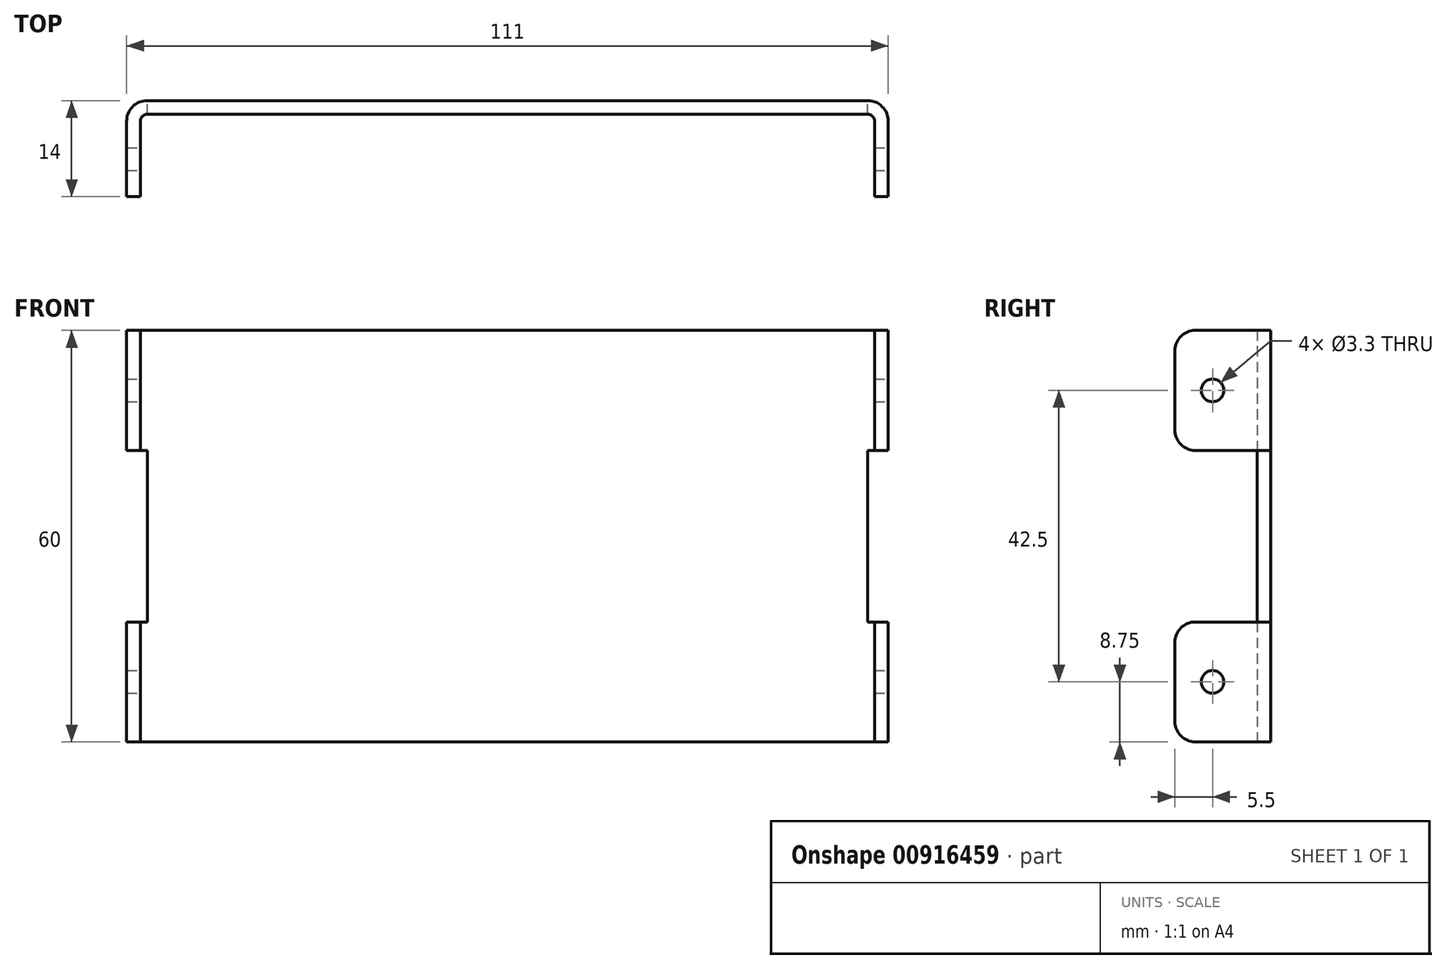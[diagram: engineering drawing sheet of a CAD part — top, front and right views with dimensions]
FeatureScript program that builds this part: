
annotation { "Feature Type Name" : "Feature", "Feature Type Description" : "" }
export const myFeature = defineFeature(function(context is Context, id is Id, definition is map)
    precondition{}
    {
        {
            var Q0;
            Q0=qCreatedBy(makeId("Top.planeOp"),FACE);
            var sketch = newSketch(context, id + "F0", { "sketchPlane" : qUnion([Q0])});
            skLineSegment(sketch, "E0", {"start": v(52.5, 0) * mm, "end": v(-52.5, 0) * mm});
            skLineSegment(sketch, "E1", {"start": v(-53.5, -1) * mm, "end": v(-53.5, -12) * mm});
            skLineSegment(sketch, "E2", {"start": v(53.5, -1) * mm, "end": v(53.5, -12) * mm});
            skPoint(sketch, "E3", {"position": v(0, 0) * mm});
            skPoint(sketch, "E4.visualSharp", {"position": v(-53.5, 0) * mm});
            skArc(sketch, "E4.filletArc", {"start": v(-52.5, 0) * mm, "mid": v(-53.2, -0.3) * mm, "end": v(-53.5, -1) * mm});
            skPoint(sketch, "E5.visualSharp", {"position": v(53.5, 0) * mm});
            skArc(sketch, "E5.filletArc", {"start": v(53.5, -1) * mm, "mid": v(53.2, -0.3) * mm, "end": v(52.5, 0) * mm});
            skLineSegment(sketch, "E6.0", {"start": v(-55.5, -1) * mm, "end": v(-55.5, -12) * mm});
            skLineSegment(sketch, "E6.1", {"start": v(55.5, -1) * mm, "end": v(55.5, -12) * mm});
            skArc(sketch, "E6.2", {"start": v(55.5, -1) * mm, "mid": v(54.62, 1.12) * mm, "end": v(52.5, 2) * mm});
            skLineSegment(sketch, "E6.3", {"start": v(52.5, 2) * mm, "end": v(-52.5, 2) * mm});
            skArc(sketch, "E6.4", {"start": v(-52.5, 2) * mm, "mid": v(-54.62, 1.12) * mm, "end": v(-55.5, -1) * mm});
            skLineSegment(sketch, "E7", {"start": v(-55.5, -12) * mm, "end": v(-53.5, -12) * mm});
            skLineSegment(sketch, "E8", {"start": v(53.5, -12) * mm, "end": v(55.5, -12) * mm});
            skSolve(sketch);
        }
        {
            var Q0;
            Q0=makeQuery(id+"F0.imprint","IMPRINT",FACE,{"disambiguationData":[TD([[makeQuery(id+"F0.imprint","IMPRINT",EDGE,{"derivedFrom":sQuery(id+"F0.wireOp",EDGE,"E0")}),-1.0]])]});
            extrude(context, id + "F1", {"entities" : qUnion([Q0]), "endBound" : BoundingType.SYMMETRIC, "depth" : 60 * mm});
        }
        {
            var Q0;
            Q0=makeQuery(id+"F1.opExtrude","SWEPT_FACE",FACE,{"disambiguationData":[OSD([sQuery(id+"F0.wireOp",EDGE,"E6.3")])]});
            var sketch = newSketch(context, id + "F2", { "sketchPlane" : qUnion([Q0])});
            skLineSegment(sketch, "E9.0", {"start": v(-55.5, 30) * mm, "end": v(-55.5, -30) * mm, "construction": true});
            skLineSegment(sketch, "E10.0", {"start": v(55.5, 30) * mm, "end": v(55.5, -30) * mm, "construction": true});
            skLineSegment(sketch, "E11.bottom", {"start": v(-55.5, 12.5) * mm, "end": v(-52.5, 12.5) * mm});
            skLineSegment(sketch, "E11.top", {"start": v(-55.5, -12.5) * mm, "end": v(-52.5, -12.5) * mm});
            skLineSegment(sketch, "E11.left", {"start": v(-55.5, 12.5) * mm, "end": v(-55.5, -12.5) * mm});
            skLineSegment(sketch, "E11.right", {"start": v(-52.5, 12.5) * mm, "end": v(-52.5, -12.5) * mm});
            skPoint(sketch, "E12", {"position": v(-52.5, 0) * mm});
            skLineSegment(sketch, "E13.MirrorCS", {"start": v(55.5, 12.5) * mm, "end": v(52.5, 12.5) * mm});
            skLineSegment(sketch, "E14.MirrorCS", {"start": v(55.5, -12.5) * mm, "end": v(52.5, -12.5) * mm});
            skPoint(sketch, "E15.MirrorP", {"position": v(52.5, 0) * mm});
            skLineSegment(sketch, "E16.MirrorCS", {"start": v(55.5, 12.5) * mm, "end": v(55.5, -12.5) * mm});
            skLineSegment(sketch, "E17.MirrorCS", {"start": v(52.5, 12.5) * mm, "end": v(52.5, -12.5) * mm});
            skPoint(sketch, "E18", {"position": v(0, 26) * mm});
            skLineSegment(sketch, "E19.bottom", {"start": v(-21.81, 24.35) * mm, "end": v(-9.8, 24.35) * mm});
            skLineSegment(sketch, "E19.top", {"start": v(-21.81, 13.85) * mm, "end": v(-9.8, 13.85) * mm});
            skLineSegment(sketch, "E19.left", {"start": v(-21.81, 24.35) * mm, "end": v(-21.81, 13.85) * mm});
            skLineSegment(sketch, "E19.right", {"start": v(-9.8, 24.35) * mm, "end": v(-9.8, 13.85) * mm});
            skLineSegment(sketch, "E20.bottom", {"start": v(9.8, 24.35) * mm, "end": v(18.96, 24.35) * mm});
            skLineSegment(sketch, "E20.top", {"start": v(9.81, 13.15) * mm, "end": v(18.96, 13.15) * mm});
            skLineSegment(sketch, "E20.left", {"start": v(9.8, 24.35) * mm, "end": v(9.81, 13.15) * mm});
            skLineSegment(sketch, "E20.right", {"start": v(18.96, 24.35) * mm, "end": v(18.96, 13.15) * mm});
            skPoint(sketch, "E21", {"position": v(0, 24.35) * mm});
            skLineSegment(sketch, "E22.bottom", {"start": v(-24.61, 11.55) * mm, "end": v(27.62, 11.55) * mm});
            skLineSegment(sketch, "E22.top", {"start": v(-24.61, 1.55) * mm, "end": v(27.62, 1.55) * mm});
            skLineSegment(sketch, "E22.left", {"start": v(-24.61, 11.55) * mm, "end": v(-24.61, 1.55) * mm});
            skLineSegment(sketch, "E22.right", {"start": v(27.62, 11.55) * mm, "end": v(27.62, 1.55) * mm});
            skSolve(sketch);
        }
        {
            var Q0;
            Q0=makeQuery(id+"F2.imprint","IMPRINT",FACE,{"disambiguationData":[TD([[makeQuery(id+"F2.imprint","IMPRINT",EDGE,{"derivedFrom":sQuery(id+"F2.wireOp",EDGE,"E11.bottom")}),-1.0]])]});
            var Q1;
            Q1=makeQuery(id+"F2.imprint","IMPRINT",FACE,{"disambiguationData":[TD([[makeQuery(id+"F2.imprint","IMPRINT",EDGE,{"derivedFrom":sQuery(id+"F2.wireOp",EDGE,"E13.MirrorCS")}),1.0]])]});
            var Q2;
            Q2=makeQuery(id+"F1.opExtrude","SWEPT_FACE",FACE,{"disambiguationData":[OSD([sQuery(id+"F0.wireOp",EDGE,"E0")])]});
            extrude(context, id + "F3", {"entities" : qUnion([Q0, Q1, Q2]), "operationType" : NewBodyOperationType.REMOVE, "endBound" : BoundingType.THROUGH_ALL, "oppositeDirection" : true, "offsetDistance" : 25 * mm, "depth" : 25 * mm});
        }
        {
            var Q0;
            {var subQ2=sQuery(id+"F0.wireOp",EDGE,"E6.1");Q0=makeQuery(id+"F3.boolean.opBoolean","SPLIT",FACE,{"disambiguationData":[TD([makeQuery(id+"F3.opExtrude","SWEPT_FACE",FACE,{"disambiguationData":[OSD([sQuery(id+"F2.wireOp",EDGE,"E11.bottom")])]})])],"derivedFrom":makeQuery(id+"F1.opExtrude","SWEPT_FACE",FACE,{"disambiguationData":[OSD([subQ2])]})});}
            var sketch = newSketch(context, id + "F4", { "sketchPlane" : qUnion([Q0])});
            skLineSegment(sketch, "E23", {"start": v(-1, 12.5) * mm, "end": v(-12, 30) * mm, "construction": true});
            skLineSegment(sketch, "E24.0.0", {"start": v(-1, -12.5) * mm, "end": v(-12, -12.5) * mm, "construction": true});
            skLineSegment(sketch, "E24.0.1", {"start": v(-12, -12.5) * mm, "end": v(-12, -30) * mm, "construction": true});
            skLineSegment(sketch, "E24.0.2", {"start": v(-12, -30) * mm, "end": v(-1, -30) * mm, "construction": true});
            skLineSegment(sketch, "E24.0.3", {"start": v(-1, -30) * mm, "end": v(-1, -12.5) * mm, "construction": true});
            skLineSegment(sketch, "E25", {"start": v(-1, -30) * mm, "end": v(-12, -12.5) * mm, "construction": true});
            skPoint(sketch, "E26", {"position": v(-6.5, 21.25) * mm});
            skPoint(sketch, "E27", {"position": v(-6.5, -21.25) * mm});
            skSolve(sketch);
        }
        {
            var Q0;
            Q0=sQuery(id+"F4.wireOp",VERTEX,"E26");
            var Q1;
            Q1=sQuery(id+"F4.wireOp",VERTEX,"E27");
            var Q2;
            Q2=makeQuery(id+"F1.opExtrude","SWEPT_BODY",BODY,{"disambiguationData":[OSD([sQuery(id+"F0.wireOp",EDGE,"E0"),sQuery(id+"F0.wireOp",EDGE,"E1"),sQuery(id+"F0.wireOp",EDGE,"E2"),sQuery(id+"F0.wireOp",EDGE,"E4.filletArc"),sQuery(id+"F0.wireOp",EDGE,"E5.filletArc"),sQuery(id+"F0.wireOp",EDGE,"E6.0"),sQuery(id+"F0.wireOp",EDGE,"E6.1"),sQuery(id+"F0.wireOp",EDGE,"E6.2"),sQuery(id+"F0.wireOp",EDGE,"E6.3"),sQuery(id+"F0.wireOp",EDGE,"E6.4"),sQuery(id+"F0.wireOp",EDGE,"E7"),sQuery(id+"F0.wireOp",EDGE,"E8")])]});
            hole(context, id + "F5", {"style" : HoleStyle.SIMPLE, "endStyle" : HoleEndStyle.THROUGH, "standardTappedOrClearance" : lookupTablePath({ "standard" : "ISO", "fit" : "Normal", "size" : "M3", "type" : "Clearance" }), "standardBlindInLast" : lookupTablePath({ "fit" : "Standard", "standard" : "ISO", "size" : "M3", "type" : "Clearance" }), "holeDiameter" : 3.3 * mm, "tappedDepth" : 12 * mm, "tapClearance" : 3, "locations" : qUnion([Q0, Q1]), "scope" : qUnion([Q2])});
        }
        {
            var Q0;
            Q0=makeQuery(id+"F1.opExtrude","CAP_EDGE",EDGE,{"disambiguationData":[OSD([sQuery(id+"F0.wireOp",EDGE,"E7")])],"isStart":false});
            var Q1;
            Q1=makeQuery(id+"F3.boolean.opBoolean","INTERSECT",EDGE,{"derivedFrom":[makeQuery(id+"F1.opExtrude","SWEPT_FACE",FACE,{"disambiguationData":[OSD([sQuery(id+"F0.wireOp",EDGE,"E7")])]}),makeQuery(id+"F3.opExtrude","SWEPT_FACE",FACE,{"disambiguationData":[OSD([sQuery(id+"F2.wireOp",EDGE,"E13.MirrorCS")])]})]});
            var Q2;
            Q2=makeQuery(id+"F3.boolean.opBoolean","INTERSECT",EDGE,{"derivedFrom":[makeQuery(id+"F1.opExtrude","SWEPT_FACE",FACE,{"disambiguationData":[OSD([sQuery(id+"F0.wireOp",EDGE,"E7")])]}),makeQuery(id+"F3.opExtrude","SWEPT_FACE",FACE,{"disambiguationData":[OSD([sQuery(id+"F2.wireOp",EDGE,"E14.MirrorCS")])]})]});
            var Q3;
            Q3=makeQuery(id+"F1.opExtrude","CAP_EDGE",EDGE,{"disambiguationData":[OSD([sQuery(id+"F0.wireOp",EDGE,"E7")])],"isStart":true});
            var Q4;
            Q4=makeQuery(id+"F1.opExtrude","CAP_EDGE",EDGE,{"disambiguationData":[OSD([sQuery(id+"F0.wireOp",EDGE,"E8")])],"isStart":false});
            var Q5;
            Q5=makeQuery(id+"F3.boolean.opBoolean","INTERSECT",EDGE,{"derivedFrom":[makeQuery(id+"F1.opExtrude","SWEPT_FACE",FACE,{"disambiguationData":[OSD([sQuery(id+"F0.wireOp",EDGE,"E8")])]}),makeQuery(id+"F3.opExtrude","SWEPT_FACE",FACE,{"disambiguationData":[OSD([sQuery(id+"F2.wireOp",EDGE,"E11.bottom")])]})]});
            var Q6;
            Q6=makeQuery(id+"F3.boolean.opBoolean","INTERSECT",EDGE,{"derivedFrom":[makeQuery(id+"F1.opExtrude","SWEPT_FACE",FACE,{"disambiguationData":[OSD([sQuery(id+"F0.wireOp",EDGE,"E8")])]}),makeQuery(id+"F3.opExtrude","SWEPT_FACE",FACE,{"disambiguationData":[OSD([sQuery(id+"F2.wireOp",EDGE,"E11.top")])]})]});
            var Q7;
            Q7=makeQuery(id+"F1.opExtrude","CAP_EDGE",EDGE,{"disambiguationData":[OSD([sQuery(id+"F0.wireOp",EDGE,"E8")])],"isStart":true});
            fillet(context, id + "F6", {"entities" : qUnion([Q0, Q1, Q2, Q3, Q4, Q5, Q6, Q7]), "radius" : 3 * mm, "tangentPropagation" : true, "allowEdgeOverflow" : false});
        }
    });
